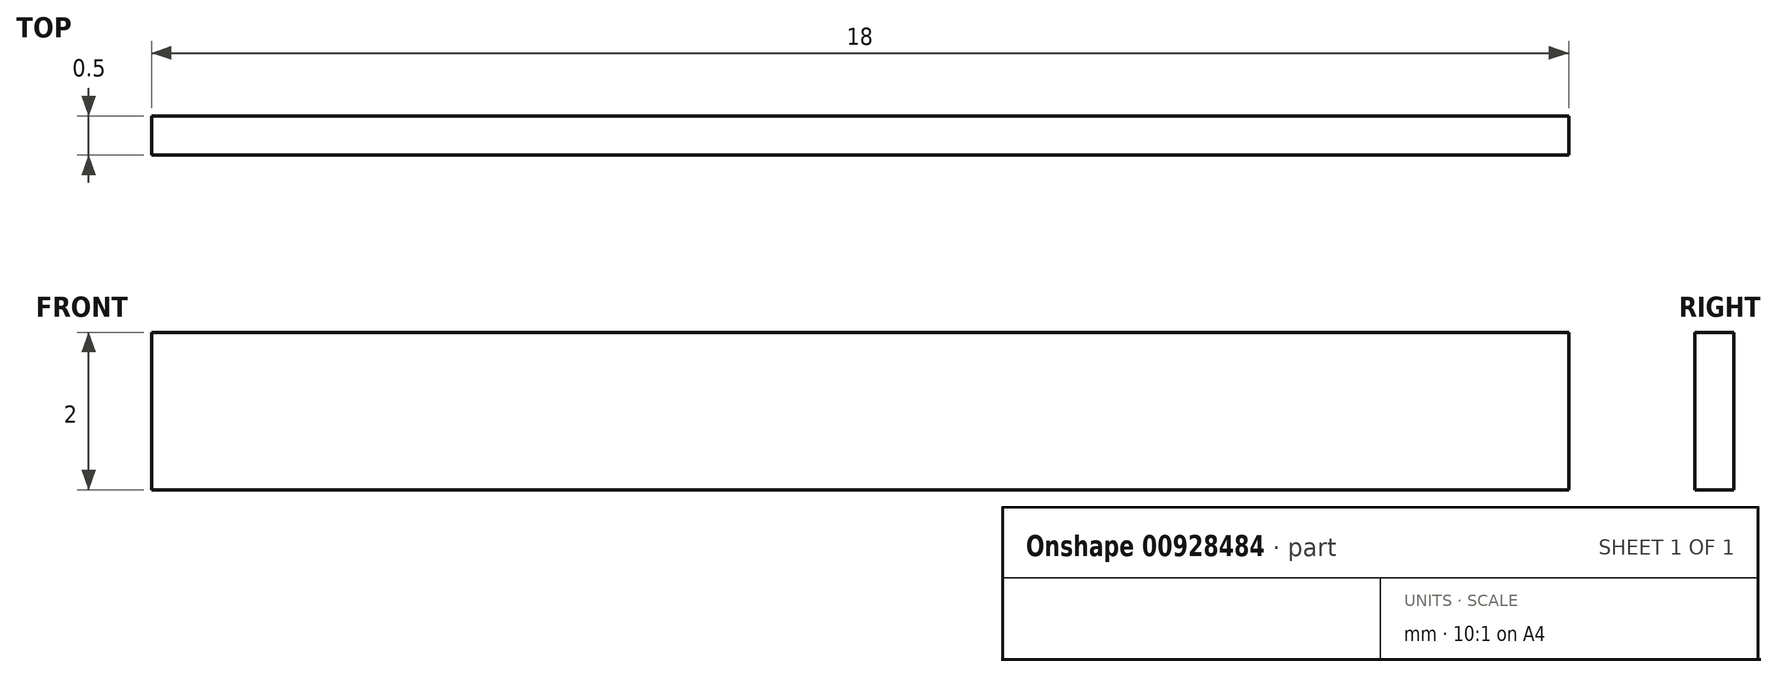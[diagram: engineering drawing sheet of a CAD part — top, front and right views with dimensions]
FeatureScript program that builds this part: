
annotation { "Feature Type Name" : "Feature", "Feature Type Description" : "" }
export const myFeature = defineFeature(function(context is Context, id is Id, definition is map)
    precondition{}
    {
        {
            var Q0;
            Q0=qCreatedBy(makeId("Front.planeOp"),FACE);
            var sketch = newSketch(context, id + "F0", { "sketchPlane" : qUnion([Q0])});
            skLineSegment(sketch, "E0.bottom", {"start": v(9, 1) * mm, "end": v(-9, 1) * mm});
            skLineSegment(sketch, "E0.top", {"start": v(9, -1) * mm, "end": v(-9, -1) * mm});
            skLineSegment(sketch, "E0.left", {"start": v(9, 1) * mm, "end": v(9, -1) * mm});
            skLineSegment(sketch, "E0.right", {"start": v(-9, 1) * mm, "end": v(-9, -1) * mm});
            skPoint(sketch, "E0.middle", {"position": v(0, 0) * mm});
            skSolve(sketch);
        }
        {
            var Q0;
            Q0=makeQuery(id+"F0.imprint","IMPRINT",FACE,{"disambiguationData":[TD([[makeQuery(id+"F0.imprint","IMPRINT",EDGE,{"derivedFrom":sQuery(id+"F0.wireOp",EDGE,"E0.bottom")}),1.0]])]});
            extrude(context, id + "F1", {"entities" : qUnion([Q0]), "depth" : 0.5 * mm, "offsetDistance" : 25 * mm});
        }
    });
